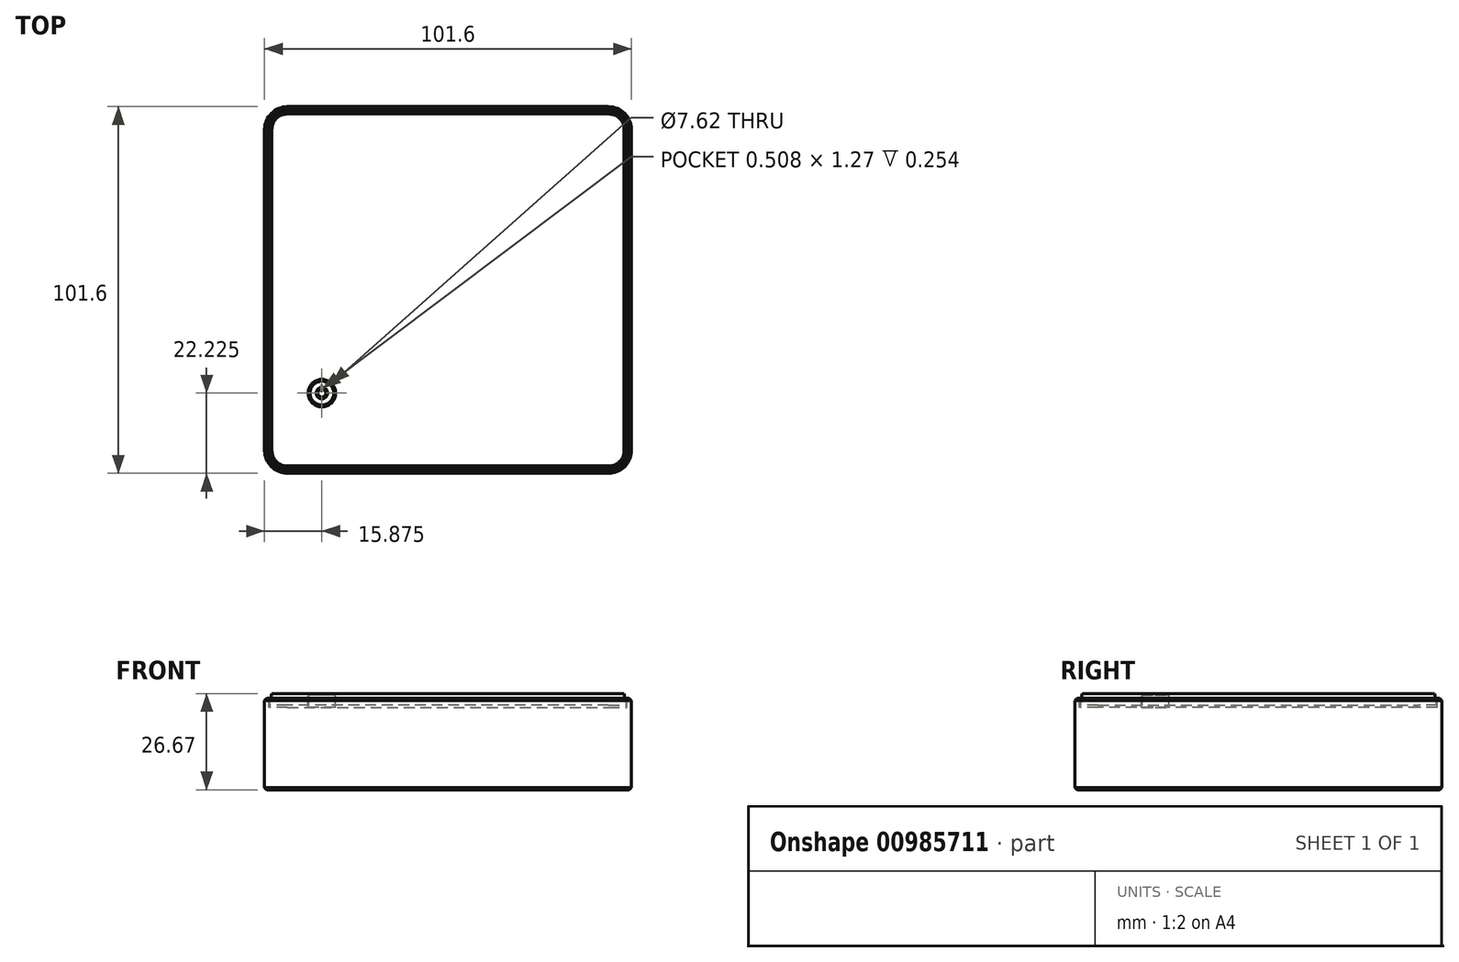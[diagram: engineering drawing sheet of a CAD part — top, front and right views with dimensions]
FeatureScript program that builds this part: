
annotation { "Feature Type Name" : "Feature", "Feature Type Description" : "" }
export const myFeature = defineFeature(function(context is Context, id is Id, definition is map)
    precondition{}
    {
        {
            var Q0;
            Q0=qCreatedBy(makeId("Top.planeOp"),FACE);
            var sketch = newSketch(context, id + "F0", { "sketchPlane" : qUnion([Q0])});
            skLineSegment(sketch, "E0.bottom", {"start": v(-50.8, 50.8) * mm, "end": v(50.8, 50.8) * mm});
            skLineSegment(sketch, "E0.top", {"start": v(-50.8, -50.8) * mm, "end": v(50.8, -50.8) * mm});
            skLineSegment(sketch, "E0.left", {"start": v(-50.8, 50.8) * mm, "end": v(-50.8, -50.8) * mm});
            skLineSegment(sketch, "E0.right", {"start": v(50.8, 50.8) * mm, "end": v(50.8, -50.8) * mm});
            skPoint(sketch, "E0.middle", {"position": v(0, 0) * mm});
            skSolve(sketch);
        }
        {
            var Q0;
            Q0 = qSketchRegion(id + "F0", true);
            extrude(context, id + "F1", {"entities" : qUnion([Q0]), "depth" : 25.4 * mm, "offsetDistance" : 25.4 * mm, "symmetric" : true});
        }
        {
            var Q0;
            Q0=makeQuery(id+"F1.opExtrude","SWEPT_EDGE",EDGE,{"disambiguationData":[OSD([sQuery(id+"F0.wireOp",EDGE,"E0.bottom"),sQuery(id+"F0.wireOp",EDGE,"E0.left")])]});
            var Q1;
            Q1=makeQuery(id+"F1.opExtrude","SWEPT_EDGE",EDGE,{"disambiguationData":[OSD([sQuery(id+"F0.wireOp",EDGE,"E0.bottom"),sQuery(id+"F0.wireOp",EDGE,"E0.right")])]});
            var Q2;
            Q2=makeQuery(id+"F1.opExtrude","SWEPT_EDGE",EDGE,{"disambiguationData":[OSD([sQuery(id+"F0.wireOp",EDGE,"E0.top"),sQuery(id+"F0.wireOp",EDGE,"E0.right")])]});
            var Q3;
            Q3=makeQuery(id+"F1.opExtrude","SWEPT_EDGE",EDGE,{"disambiguationData":[OSD([sQuery(id+"F0.wireOp",EDGE,"E0.top"),sQuery(id+"F0.wireOp",EDGE,"E0.left")])]});
            fillet(context, id + "F2", {"entities" : qUnion([Q0, Q1, Q2, Q3]), "tangentPropagation" : true, "radius" : 6.35 * mm, "defaultsChanged" : true, "vertexSettings" : [], "allowEdgeOverflow" : false});
        }
        {
            var Q0;
            Q0=makeQuery(id+"F1.opExtrude","CAP_FACE",FACE,{"disambiguationData":[OSD([sQuery(id+"F0.wireOp",EDGE,"E0.bottom"),sQuery(id+"F0.wireOp",EDGE,"E0.top"),sQuery(id+"F0.wireOp",EDGE,"E0.left"),sQuery(id+"F0.wireOp",EDGE,"E0.right")])],"isStart":false});
            var sketch = newSketch(context, id + "F3", { "sketchPlane" : qUnion([Q0])});
            skArc(sketch, "E1.0", {"start": v(-44.45, 49.53) * mm, "mid": v(-48.04, 48.04) * mm, "end": v(-49.53, 44.45) * mm});
            skLineSegment(sketch, "E1.1", {"start": v(-49.53, 44.45) * mm, "end": v(-49.53, -44.45) * mm});
            skLineSegment(sketch, "E1.2", {"start": v(-44.45, 49.53) * mm, "end": v(44.45, 49.53) * mm});
            skArc(sketch, "E1.3", {"start": v(-49.53, -44.45) * mm, "mid": v(-48.04, -48.04) * mm, "end": v(-44.45, -49.53) * mm});
            skArc(sketch, "E1.4", {"start": v(49.53, 44.45) * mm, "mid": v(48.04, 48.04) * mm, "end": v(44.45, 49.53) * mm});
            skLineSegment(sketch, "E1.5", {"start": v(49.53, 44.45) * mm, "end": v(49.53, -44.45) * mm});
            skArc(sketch, "E1.6", {"start": v(44.45, -49.53) * mm, "mid": v(48.04, -48.04) * mm, "end": v(49.53, -44.45) * mm});
            skLineSegment(sketch, "E1.7", {"start": v(-44.45, -49.53) * mm, "end": v(44.45, -49.53) * mm});
            skSolve(sketch);
        }
        {
            var Q0;
            Q0 = qSketchRegion(id + "F3", true);
            extrude(context, id + "F4", {"entities" : qUnion([Q0]), "operationType" : NewBodyOperationType.REMOVE, "oppositeDirection" : true, "depth" : 2.54 * mm, "offsetDistance" : 25.4 * mm});
        }
        {
            var Q0;
            Q0=makeQuery(id+"F4.boolean.opBoolean","COPY",FACE,{"derivedFrom":makeQuery(id+"F4.opExtrude","CAP_FACE",FACE,{"disambiguationData":[OSD([sQuery(id+"F3.wireOp",EDGE,"E1.0"),sQuery(id+"F3.wireOp",EDGE,"E1.1"),sQuery(id+"F3.wireOp",EDGE,"E1.2"),sQuery(id+"F3.wireOp",EDGE,"E1.3"),sQuery(id+"F3.wireOp",EDGE,"E1.4"),sQuery(id+"F3.wireOp",EDGE,"E1.5"),sQuery(id+"F3.wireOp",EDGE,"E1.6"),sQuery(id+"F3.wireOp",EDGE,"E1.7")])],"isStart":false})});
            var sketch = newSketch(context, id + "F5", { "sketchPlane" : qUnion([Q0])});
            skLineSegment(sketch, "E2.0", {"start": v(-49.4, 44.45) * mm, "end": v(-49.4, -44.45) * mm});
            skArc(sketch, "E2.1", {"start": v(-44.45, 49.4) * mm, "mid": v(-47.95, 47.95) * mm, "end": v(-49.4, 44.45) * mm});
            skArc(sketch, "E2.2", {"start": v(-49.4, -44.45) * mm, "mid": v(-47.95, -47.95) * mm, "end": v(-44.45, -49.4) * mm});
            skLineSegment(sketch, "E2.3", {"start": v(44.45, 49.4) * mm, "end": v(-44.45, 49.4) * mm});
            skLineSegment(sketch, "E2.4", {"start": v(-44.45, -49.4) * mm, "end": v(44.45, -49.4) * mm});
            skArc(sketch, "E2.5", {"start": v(44.45, -49.4) * mm, "mid": v(47.95, -47.95) * mm, "end": v(49.4, -44.45) * mm});
            skLineSegment(sketch, "E2.6", {"start": v(49.4, -44.45) * mm, "end": v(49.4, 44.45) * mm});
            skArc(sketch, "E2.7", {"start": v(49.4, 44.45) * mm, "mid": v(47.95, 47.95) * mm, "end": v(44.45, 49.4) * mm});
            skSolve(sketch);
        }
        {
            var Q0;
            Q0=makeQuery(id+"F5.imprint","IMPRINT",FACE,{"disambiguationData":[TD([[makeQuery(id+"F5.imprint","IMPRINT",EDGE,{"derivedFrom":sQuery(id+"F5.wireOp",EDGE,"E2.0")}),1.0]])]});
            extrude(context, id + "F6", {"entities" : qUnion([Q0]), "depth" : 3.8 * mm, "offsetDistance" : 25.4 * mm});
        }
        {
            var Q0;
            Q0=makeQuery(id+"F1.opExtrude","CAP_EDGE",EDGE,{"disambiguationData":[OSD([sQuery(id+"F0.wireOp",EDGE,"E0.left")])],"isStart":false});
            var Q1;
            {var subQ0=sQuery(id+"F0.wireOp",EDGE,"E0.left");var subQ1=sQuery(id+"F0.wireOp",EDGE,"E0.bottom");Q1=makeQuery(id+"F2.opFillet","BLEND_EDGE",EDGE,{"blendedFrom":[makeQuery(id+"F1.opExtrude","SWEPT_EDGE",EDGE,{"disambiguationData":[OSD([subQ1,subQ0])]}),makeQuery(id+"F1.opExtrude","CAP_FACE",FACE,{"disambiguationData":[OSD([subQ1,sQuery(id+"F0.wireOp",EDGE,"E0.top"),subQ0,sQuery(id+"F0.wireOp",EDGE,"E0.right")])],"isStart":false})],"blendedInto":[makeQuery(id+"F1.opExtrude","CAP_FACE",FACE,{"disambiguationData":[OSD([subQ1,sQuery(id+"F0.wireOp",EDGE,"E0.top"),subQ0,sQuery(id+"F0.wireOp",EDGE,"E0.right")])],"isStart":false})]});}
            var Q2;
            Q2=makeQuery(id+"F1.opExtrude","CAP_EDGE",EDGE,{"disambiguationData":[OSD([sQuery(id+"F0.wireOp",EDGE,"E0.bottom")])],"isStart":false});
            var Q3;
            {var subQ0=sQuery(id+"F0.wireOp",EDGE,"E0.right");var subQ1=sQuery(id+"F0.wireOp",EDGE,"E0.bottom");Q3=makeQuery(id+"F2.opFillet","BLEND_EDGE",EDGE,{"blendedFrom":[makeQuery(id+"F1.opExtrude","SWEPT_EDGE",EDGE,{"disambiguationData":[OSD([subQ1,subQ0])]}),makeQuery(id+"F1.opExtrude","CAP_FACE",FACE,{"disambiguationData":[OSD([subQ1,sQuery(id+"F0.wireOp",EDGE,"E0.top"),sQuery(id+"F0.wireOp",EDGE,"E0.left"),subQ0])],"isStart":false})],"blendedInto":[makeQuery(id+"F1.opExtrude","CAP_FACE",FACE,{"disambiguationData":[OSD([subQ1,sQuery(id+"F0.wireOp",EDGE,"E0.top"),sQuery(id+"F0.wireOp",EDGE,"E0.left"),subQ0])],"isStart":false})]});}
            var Q4;
            Q4=makeQuery(id+"F1.opExtrude","CAP_EDGE",EDGE,{"disambiguationData":[OSD([sQuery(id+"F0.wireOp",EDGE,"E0.left")])],"isStart":true});
            chamfer(context, id + "F7", {"entities" : qUnion([Q0, Q1, Q2, Q3, Q4]), "width" : 0.64 * mm, "tangentPropagation" : true});
        }
        {
            var Q0;
            Q0=makeQuery(id+"F6.opExtrude","CAP_EDGE",EDGE,{"disambiguationData":[OSD([sQuery(id+"F5.wireOp",EDGE,"E2.0")])],"isStart":false});
            chamfer(context, id + "F8", {"entities" : qUnion([Q0]), "chamferType" : ChamferType.TWO_OFFSETS, "width1" : 0.64 * mm, "oppositeDirection" : true, "width2" : 3.17 * mm, "tangentPropagation" : true});
        }
        {
            var Q0;
            Q0=makeQuery(id+"F6.opExtrude","CAP_FACE",FACE,{"disambiguationData":[OSD([sQuery(id+"F5.wireOp",EDGE,"E2.0"),sQuery(id+"F5.wireOp",EDGE,"E2.1"),sQuery(id+"F5.wireOp",EDGE,"E2.2"),sQuery(id+"F5.wireOp",EDGE,"E2.3"),sQuery(id+"F5.wireOp",EDGE,"E2.4"),sQuery(id+"F5.wireOp",EDGE,"E2.5"),sQuery(id+"F5.wireOp",EDGE,"E2.6"),sQuery(id+"F5.wireOp",EDGE,"E2.7")])],"isStart":false});
            var sketch = newSketch(context, id + "F9", { "sketchPlane" : qUnion([Q0])});
            skCircle(sketch, "E3", {"center": v(-34.93, -28.57) * mm, "radius": 3.8 * mm});
            skLineSegment(sketch, "E4", {"start": v(-50.8, -28.57) * mm, "end": v(-34.93, -28.57) * mm, "construction": true});
            skLineSegment(sketch, "E5", {"start": v(-34.93, -50.8) * mm, "end": v(-34.93, -28.57) * mm, "construction": true});
            skSolve(sketch);
        }
        {
            var Q0;
            Q0=makeQuery(id+"F9.imprint","IMPRINT",FACE,{"disambiguationData":[TD([[makeQuery(id+"F9.imprint","IMPRINT",EDGE,{"derivedFrom":sQuery(id+"F9.wireOp",EDGE,"E3")}),1.0]])]});
            extrude(context, id + "F10", {"entities" : qUnion([Q0]), "operationType" : NewBodyOperationType.REMOVE, "oppositeDirection" : true, "depth" : 3.8 * mm, "offsetDistance" : 25.4 * mm});
        }
        {
            var Q0;
            Q0=makeQuery(id+"F4.boolean.opBoolean","COPY",FACE,{"derivedFrom":makeQuery(id+"F4.opExtrude","CAP_FACE",FACE,{"disambiguationData":[OSD([sQuery(id+"F3.wireOp",EDGE,"E1.0"),sQuery(id+"F3.wireOp",EDGE,"E1.1"),sQuery(id+"F3.wireOp",EDGE,"E1.2"),sQuery(id+"F3.wireOp",EDGE,"E1.3"),sQuery(id+"F3.wireOp",EDGE,"E1.4"),sQuery(id+"F3.wireOp",EDGE,"E1.5"),sQuery(id+"F3.wireOp",EDGE,"E1.6"),sQuery(id+"F3.wireOp",EDGE,"E1.7")])],"isStart":false})});
            var sketch = newSketch(context, id + "F11", { "sketchPlane" : qUnion([Q0])});
            skCircle(sketch, "E6.0", {"center": v(-34.93, -28.57) * mm, "radius": 3.68 * mm});
            skSolve(sketch);
        }
        {
            var Q0;
            Q0 = qSketchRegion(id + "F11", true);
            extrude(context, id + "F12", {"entities" : qUnion([Q0]), "operationType" : NewBodyOperationType.ADD, "depth" : 3.8 * mm, "offsetDistance" : 25.4 * mm});
        }
        {
            var Q0;
            Q0=makeQuery(id+"F12.opExtrude","CAP_EDGE",EDGE,{"disambiguationData":[OSD([sQuery(id+"F11.wireOp",EDGE,"E6.0")])],"isStart":false});
            chamfer(context, id + "F13", {"entities" : qUnion([Q0]), "width" : 0.38 * mm, "tangentPropagation" : true});
        }
        {
            var Q0;
            Q0=makeQuery(id+"F12.opExtrude","CAP_FACE",FACE,{"disambiguationData":[OSD([sQuery(id+"F11.wireOp",EDGE,"E6.0")])],"isStart":false});
            var sketch = newSketch(context, id + "F14", { "sketchPlane" : qUnion([Q0])});
            skLineSegment(sketch, "E7", {"start": v(-35.6, -27.14) * mm, "end": v(-35.38, -27.6) * mm});
            skLineSegment(sketch, "E8", {"start": v(-34.47, -27.6) * mm, "end": v(-34.25, -27.14) * mm});
            skLineSegment(sketch, "E9", {"start": v(-35.38, -27.6) * mm, "end": v(-34.93, -28.57) * mm, "construction": true});
            skLineSegment(sketch, "E10", {"start": v(-34.47, -27.6) * mm, "end": v(-34.93, -28.57) * mm, "construction": true});
            skLineSegment(sketch, "E11", {"start": v(-35.38, -27.6) * mm, "end": v(-35.38, -27.6) * mm});
            skPoint(sketch, "E12", {"position": v(-34.93, -27.6) * mm});
            skArc(sketch, "E13", {"start": v(-34.25, -27.14) * mm, "mid": v(-34.93, -26.99) * mm, "end": v(-35.6, -27.14) * mm, "construction": true});
            skArc(sketch, "E14", {"start": v(-35.6, -27.14) * mm, "mid": v(-34.93, -30.16) * mm, "end": v(-34.25, -27.14) * mm});
            skLineSegment(sketch, "E15", {"start": v(-35.38, -27.6) * mm, "end": v(-34.47, -27.6) * mm, "construction": true});
            skArc(sketch, "E16", {"start": v(-34.47, -27.6) * mm, "mid": v(-34.93, -27.5) * mm, "end": v(-35.38, -27.6) * mm, "construction": true});
            skArc(sketch, "E17", {"start": v(-35.38, -27.6) * mm, "mid": v(-34.93, -29.65) * mm, "end": v(-34.47, -27.6) * mm});
            skLineSegment(sketch, "E18.bottom", {"start": v(-35.18, -26.67) * mm, "end": v(-34.67, -26.67) * mm});
            skLineSegment(sketch, "E18.top", {"start": v(-35.18, -27.94) * mm, "end": v(-34.67, -27.94) * mm});
            skLineSegment(sketch, "E18.left", {"start": v(-35.18, -26.67) * mm, "end": v(-35.18, -27.94) * mm});
            skLineSegment(sketch, "E18.right", {"start": v(-34.67, -26.67) * mm, "end": v(-34.67, -27.94) * mm});
            skPoint(sketch, "E18.middle", {"position": v(-34.93, -27.3) * mm});
            skLineSegment(sketch, "E19", {"start": v(-34.93, -27.3) * mm, "end": v(-34.93, -28.57) * mm, "construction": true});
            skSolve(sketch);
        }
        {
            var Q0;
            Q0=makeQuery(id+"F14.imprint","IMPRINT",FACE,{"disambiguationData":[TD([[makeQuery(id+"F14.imprint","IMPRINT",EDGE,{"derivedFrom":sQuery(id+"F14.wireOp",EDGE,"E7")}),-1.0]])]});
            var Q1;
            Q1=makeQuery(id+"F14.imprint","IMPRINT",FACE,{"disambiguationData":[TD([[makeQuery(id+"F14.imprint","IMPRINT",EDGE,{"derivedFrom":sQuery(id+"F14.wireOp",EDGE,"E18.bottom")}),-1.0]])]});
            extrude(context, id + "F15", {"entities" : qUnion([Q0, Q1]), "operationType" : NewBodyOperationType.REMOVE, "oppositeDirection" : true, "depth" : 0.25 * mm, "offsetDistance" : 25.4 * mm});
        }
    });
